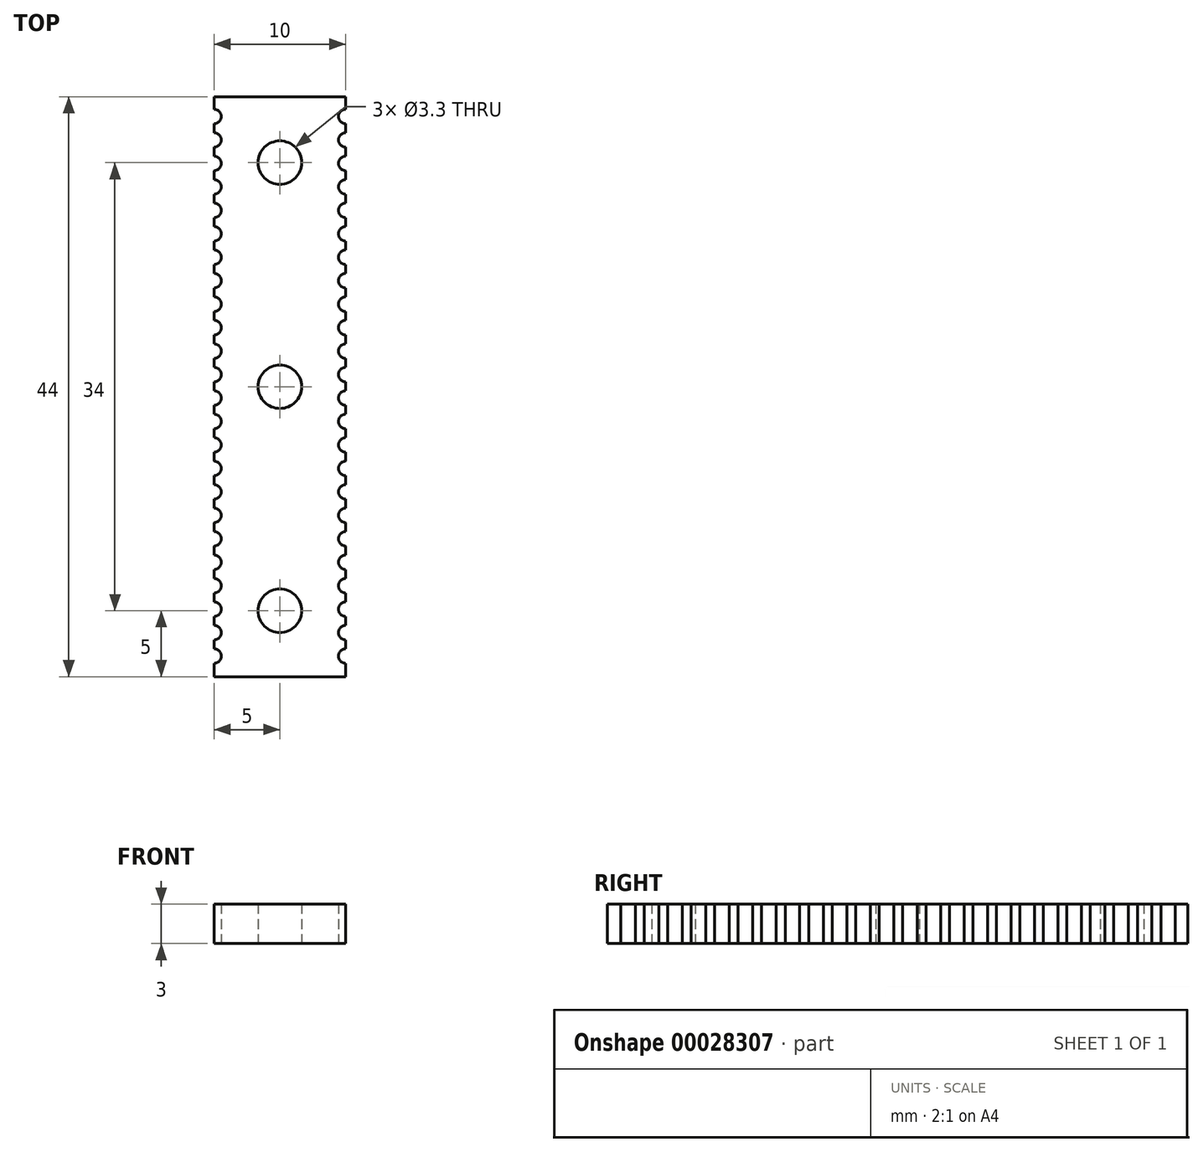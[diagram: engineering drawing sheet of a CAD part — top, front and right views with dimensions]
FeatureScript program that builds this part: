
annotation { "Feature Type Name" : "Feature", "Feature Type Description" : "" }
export const myFeature = defineFeature(function(context is Context, id is Id, definition is map)
    precondition{}
    {
        {
            var Q0;
            Q0=qCreatedBy(makeId("Top.planeOp"),FACE);
            var sketch = newSketch(context, id + "F0", { "sketchPlane" : qUnion([Q0])});
            skLineSegment(sketch, "E0.bottom", {"start": v(0, 0) * mm, "end": v(10, 0) * mm});
            skLineSegment(sketch, "E0.top", {"start": v(0, 44) * mm, "end": v(10, 44) * mm});
            skLineSegment(sketch, "E0.left", {"start": v(0, 0) * mm, "end": v(0, 44) * mm});
            skLineSegment(sketch, "E0.right", {"start": v(10, 0) * mm, "end": v(10, 44) * mm});
            skCircle(sketch, "E1", {"center": v(0, 42.5) * mm, "radius": 0.55 * mm});
            skCircle(sketch, "E2.0.1.0", {"center": v(0, 40.72) * mm, "radius": 0.55 * mm});
            skCircle(sketch, "E2.0.2.0", {"center": v(0, 38.94) * mm, "radius": 0.55 * mm});
            skCircle(sketch, "E2.0.3.0", {"center": v(0, 37.16) * mm, "radius": 0.55 * mm});
            skCircle(sketch, "E2.0.4.0", {"center": v(0, 35.38) * mm, "radius": 0.55 * mm});
            skCircle(sketch, "E2.0.5.0", {"center": v(0, 33.6) * mm, "radius": 0.55 * mm});
            skCircle(sketch, "E2.0.6.0", {"center": v(0, 31.82) * mm, "radius": 0.55 * mm});
            skCircle(sketch, "E2.0.7.0", {"center": v(0, 30.04) * mm, "radius": 0.55 * mm});
            skCircle(sketch, "E2.0.8.0", {"center": v(0, 28.26) * mm, "radius": 0.55 * mm});
            skCircle(sketch, "E2.0.9.0", {"center": v(0, 26.48) * mm, "radius": 0.55 * mm});
            skCircle(sketch, "E2.0.10.0", {"center": v(0, 24.7) * mm, "radius": 0.55 * mm});
            skCircle(sketch, "E2.0.11.0", {"center": v(0, 22.92) * mm, "radius": 0.55 * mm});
            skCircle(sketch, "E2.0.12.0", {"center": v(0, 21.14) * mm, "radius": 0.55 * mm});
            skCircle(sketch, "E2.0.13.0", {"center": v(0, 19.36) * mm, "radius": 0.55 * mm});
            skCircle(sketch, "E2.0.14.0", {"center": v(0, 17.58) * mm, "radius": 0.55 * mm});
            skCircle(sketch, "E2.0.15.0", {"center": v(0, 15.8) * mm, "radius": 0.55 * mm});
            skCircle(sketch, "E2.0.16.0", {"center": v(0, 14.02) * mm, "radius": 0.55 * mm});
            skCircle(sketch, "E2.0.17.0", {"center": v(0, 12.24) * mm, "radius": 0.55 * mm});
            skCircle(sketch, "E2.0.18.0", {"center": v(0, 10.46) * mm, "radius": 0.55 * mm});
            skCircle(sketch, "E2.0.19.0", {"center": v(0, 8.68) * mm, "radius": 0.55 * mm});
            skCircle(sketch, "E2.0.20.0", {"center": v(0, 6.9) * mm, "radius": 0.55 * mm});
            skCircle(sketch, "E2.0.21.0", {"center": v(0, 5.12) * mm, "radius": 0.55 * mm});
            skCircle(sketch, "E2.1.0.0", {"center": v(10, 42.5) * mm, "radius": 0.55 * mm});
            skCircle(sketch, "E2.1.1.0", {"center": v(10, 40.72) * mm, "radius": 0.55 * mm});
            skCircle(sketch, "E2.1.2.0", {"center": v(10, 38.94) * mm, "radius": 0.55 * mm});
            skCircle(sketch, "E2.1.3.0", {"center": v(10, 37.16) * mm, "radius": 0.55 * mm});
            skCircle(sketch, "E2.1.4.0", {"center": v(10, 35.38) * mm, "radius": 0.55 * mm});
            skCircle(sketch, "E2.1.5.0", {"center": v(10, 33.6) * mm, "radius": 0.55 * mm});
            skCircle(sketch, "E2.1.6.0", {"center": v(10, 31.82) * mm, "radius": 0.55 * mm});
            skCircle(sketch, "E2.1.7.0", {"center": v(10, 30.04) * mm, "radius": 0.55 * mm});
            skCircle(sketch, "E2.1.8.0", {"center": v(10, 28.26) * mm, "radius": 0.55 * mm});
            skCircle(sketch, "E2.1.9.0", {"center": v(10, 26.48) * mm, "radius": 0.55 * mm});
            skCircle(sketch, "E2.1.10.0", {"center": v(10, 24.7) * mm, "radius": 0.55 * mm});
            skCircle(sketch, "E2.1.11.0", {"center": v(10, 22.92) * mm, "radius": 0.55 * mm});
            skCircle(sketch, "E2.1.12.0", {"center": v(10, 21.14) * mm, "radius": 0.55 * mm});
            skCircle(sketch, "E2.1.13.0", {"center": v(10, 19.36) * mm, "radius": 0.55 * mm});
            skCircle(sketch, "E2.1.14.0", {"center": v(10, 17.58) * mm, "radius": 0.55 * mm});
            skCircle(sketch, "E2.1.15.0", {"center": v(10, 15.8) * mm, "radius": 0.55 * mm});
            skCircle(sketch, "E2.1.16.0", {"center": v(10, 14.02) * mm, "radius": 0.55 * mm});
            skCircle(sketch, "E2.1.17.0", {"center": v(10, 12.24) * mm, "radius": 0.55 * mm});
            skCircle(sketch, "E2.1.18.0", {"center": v(10, 10.46) * mm, "radius": 0.55 * mm});
            skCircle(sketch, "E2.1.19.0", {"center": v(10, 8.68) * mm, "radius": 0.55 * mm});
            skCircle(sketch, "E2.1.20.0", {"center": v(10, 6.9) * mm, "radius": 0.55 * mm});
            skCircle(sketch, "E2.1.21.0", {"center": v(10, 5.12) * mm, "radius": 0.55 * mm});
            skLineSegment(sketch, "E2.direction1", {"start": v(0, 42.5) * mm, "end": v(10, 42.5) * mm, "construction": true});
            skLineSegment(sketch, "E2.direction2", {"start": v(0, 42.5) * mm, "end": v(0, 40.72) * mm, "construction": true});
            skCircle(sketch, "E3.0.0.22", {"center": v(0, 3.34) * mm, "radius": 0.55 * mm});
            skCircle(sketch, "E3.0.0.23", {"center": v(0, 1.56) * mm, "radius": 0.55 * mm});
            skCircle(sketch, "E3.0.1.22", {"center": v(10, 3.34) * mm, "radius": 0.55 * mm});
            skCircle(sketch, "E3.0.1.23", {"center": v(10, 1.56) * mm, "radius": 0.55 * mm});
            skSolve(sketch);
        }
        {
            var Q0;
            {var subQ102=sQuery(id+"F0.wireOp",EDGE,"E0.bottom");Q0=makeQuery(id+"F0.imprint","IMPRINT",FACE,{"disambiguationData":[TD([[makeQuery(id+"F0.imprint","IMPRINT",EDGE,{"derivedFrom":subQ102}),1.0]])]});}
            var sketch = newSketch(context, id + "F1", { "sketchPlane" : qUnion([Q0])});
            skSolve(sketch);
        }
        {
            var Q0;
            Q0 = qSketchRegion(id + "F1", true);
            var Q1;
            {var subQ102=sQuery(id+"F0.wireOp",EDGE,"E0.bottom");Q1=makeQuery(id+"F0.imprint","IMPRINT",FACE,{"disambiguationData":[TD([[makeQuery(id+"F0.imprint","IMPRINT",EDGE,{"derivedFrom":subQ102}),1.0]])]});}
            extrude(context, id + "F2", {"entities" : qUnion([Q0, Q1]), "depth" : 3 * mm});
        }
        {
            var Q0;
            Q0=makeQuery(id+"F2.opExtrude","CAP_FACE",FACE,{"disambiguationData":[OSD([sQuery(id+"F0.wireOp",EDGE,"E0.bottom"),sQuery(id+"F0.wireOp",EDGE,"E0.top"),sQuery(id+"F0.wireOp",EDGE,"E0.left"),sQuery(id+"F0.wireOp",EDGE,"E0.right"),sQuery(id+"F0.wireOp",EDGE,"E1"),sQuery(id+"F0.wireOp",EDGE,"E2.0.1.0"),sQuery(id+"F0.wireOp",EDGE,"E2.0.2.0"),sQuery(id+"F0.wireOp",EDGE,"E2.0.3.0"),sQuery(id+"F0.wireOp",EDGE,"E2.0.4.0"),sQuery(id+"F0.wireOp",EDGE,"E2.0.5.0"),sQuery(id+"F0.wireOp",EDGE,"E2.0.6.0"),sQuery(id+"F0.wireOp",EDGE,"E2.0.7.0"),sQuery(id+"F0.wireOp",EDGE,"E2.0.8.0"),sQuery(id+"F0.wireOp",EDGE,"E2.0.9.0"),sQuery(id+"F0.wireOp",EDGE,"E2.0.10.0"),sQuery(id+"F0.wireOp",EDGE,"E2.0.11.0"),sQuery(id+"F0.wireOp",EDGE,"E2.0.12.0"),sQuery(id+"F0.wireOp",EDGE,"E2.0.13.0"),sQuery(id+"F0.wireOp",EDGE,"E2.0.14.0"),sQuery(id+"F0.wireOp",EDGE,"E2.0.15.0"),sQuery(id+"F0.wireOp",EDGE,"E2.0.16.0"),sQuery(id+"F0.wireOp",EDGE,"E2.0.17.0"),sQuery(id+"F0.wireOp",EDGE,"E2.0.18.0"),sQuery(id+"F0.wireOp",EDGE,"E2.0.19.0"),sQuery(id+"F0.wireOp",EDGE,"E2.0.20.0"),sQuery(id+"F0.wireOp",EDGE,"E2.0.21.0"),sQuery(id+"F0.wireOp",EDGE,"E2.1.0.0"),sQuery(id+"F0.wireOp",EDGE,"E2.1.1.0"),sQuery(id+"F0.wireOp",EDGE,"E2.1.2.0"),sQuery(id+"F0.wireOp",EDGE,"E2.1.3.0"),sQuery(id+"F0.wireOp",EDGE,"E2.1.4.0"),sQuery(id+"F0.wireOp",EDGE,"E2.1.5.0"),sQuery(id+"F0.wireOp",EDGE,"E2.1.6.0"),sQuery(id+"F0.wireOp",EDGE,"E2.1.7.0"),sQuery(id+"F0.wireOp",EDGE,"E2.1.8.0"),sQuery(id+"F0.wireOp",EDGE,"E2.1.9.0"),sQuery(id+"F0.wireOp",EDGE,"E2.1.10.0"),sQuery(id+"F0.wireOp",EDGE,"E2.1.11.0"),sQuery(id+"F0.wireOp",EDGE,"E2.1.12.0"),sQuery(id+"F0.wireOp",EDGE,"E2.1.13.0"),sQuery(id+"F0.wireOp",EDGE,"E2.1.14.0"),sQuery(id+"F0.wireOp",EDGE,"E2.1.15.0"),sQuery(id+"F0.wireOp",EDGE,"E2.1.16.0"),sQuery(id+"F0.wireOp",EDGE,"E2.1.17.0"),sQuery(id+"F0.wireOp",EDGE,"E2.1.18.0"),sQuery(id+"F0.wireOp",EDGE,"E2.1.19.0"),sQuery(id+"F0.wireOp",EDGE,"E2.1.20.0"),sQuery(id+"F0.wireOp",EDGE,"E2.1.21.0")])],"isStart":false});
            var sketch = newSketch(context, id + "F3", { "sketchPlane" : qUnion([Q0])});
            skLineSegment(sketch, "E4", {"start": v(5, 0) * mm, "end": v(5, 44) * mm, "construction": true});
            skPoint(sketch, "E5", {"position": v(5, 5) * mm});
            skPoint(sketch, "E6", {"position": v(5, 39) * mm});
            skPoint(sketch, "E7", {"position": v(5, 22) * mm});
            skSolve(sketch);
        }
        {
            var Q0;
            Q0=sQuery(id+"F3.wireOp",VERTEX,"E5");
            var Q1;
            Q1=sQuery(id+"F3.wireOp",VERTEX,"E7");
            var Q2;
            Q2=sQuery(id+"F3.wireOp",VERTEX,"E6");
            var Q3;
            Q3=makeQuery(id+"F2.opExtrude","SWEPT_BODY",BODY,{"disambiguationData":[OSD([sQuery(id+"F0.wireOp",EDGE,"E0.bottom"),sQuery(id+"F0.wireOp",EDGE,"E0.top"),sQuery(id+"F0.wireOp",EDGE,"E0.left"),sQuery(id+"F0.wireOp",EDGE,"E0.right"),sQuery(id+"F0.wireOp",EDGE,"E1"),sQuery(id+"F0.wireOp",EDGE,"E2.0.1.0"),sQuery(id+"F0.wireOp",EDGE,"E2.0.2.0"),sQuery(id+"F0.wireOp",EDGE,"E2.0.3.0"),sQuery(id+"F0.wireOp",EDGE,"E2.0.4.0"),sQuery(id+"F0.wireOp",EDGE,"E2.0.5.0"),sQuery(id+"F0.wireOp",EDGE,"E2.0.6.0"),sQuery(id+"F0.wireOp",EDGE,"E2.0.7.0"),sQuery(id+"F0.wireOp",EDGE,"E2.0.8.0"),sQuery(id+"F0.wireOp",EDGE,"E2.0.9.0"),sQuery(id+"F0.wireOp",EDGE,"E2.0.10.0"),sQuery(id+"F0.wireOp",EDGE,"E2.0.11.0"),sQuery(id+"F0.wireOp",EDGE,"E2.0.12.0"),sQuery(id+"F0.wireOp",EDGE,"E2.0.13.0"),sQuery(id+"F0.wireOp",EDGE,"E2.0.14.0"),sQuery(id+"F0.wireOp",EDGE,"E2.0.15.0"),sQuery(id+"F0.wireOp",EDGE,"E2.0.16.0"),sQuery(id+"F0.wireOp",EDGE,"E2.0.17.0"),sQuery(id+"F0.wireOp",EDGE,"E2.0.18.0"),sQuery(id+"F0.wireOp",EDGE,"E2.0.19.0"),sQuery(id+"F0.wireOp",EDGE,"E2.0.20.0"),sQuery(id+"F0.wireOp",EDGE,"E2.0.21.0"),sQuery(id+"F0.wireOp",EDGE,"E2.1.0.0"),sQuery(id+"F0.wireOp",EDGE,"E2.1.1.0"),sQuery(id+"F0.wireOp",EDGE,"E2.1.2.0"),sQuery(id+"F0.wireOp",EDGE,"E2.1.3.0"),sQuery(id+"F0.wireOp",EDGE,"E2.1.4.0"),sQuery(id+"F0.wireOp",EDGE,"E2.1.5.0"),sQuery(id+"F0.wireOp",EDGE,"E2.1.6.0"),sQuery(id+"F0.wireOp",EDGE,"E2.1.7.0"),sQuery(id+"F0.wireOp",EDGE,"E2.1.8.0"),sQuery(id+"F0.wireOp",EDGE,"E2.1.9.0"),sQuery(id+"F0.wireOp",EDGE,"E2.1.10.0"),sQuery(id+"F0.wireOp",EDGE,"E2.1.11.0"),sQuery(id+"F0.wireOp",EDGE,"E2.1.12.0"),sQuery(id+"F0.wireOp",EDGE,"E2.1.13.0"),sQuery(id+"F0.wireOp",EDGE,"E2.1.14.0"),sQuery(id+"F0.wireOp",EDGE,"E2.1.15.0"),sQuery(id+"F0.wireOp",EDGE,"E2.1.16.0"),sQuery(id+"F0.wireOp",EDGE,"E2.1.17.0"),sQuery(id+"F0.wireOp",EDGE,"E2.1.18.0"),sQuery(id+"F0.wireOp",EDGE,"E2.1.19.0"),sQuery(id+"F0.wireOp",EDGE,"E2.1.20.0"),sQuery(id+"F0.wireOp",EDGE,"E2.1.21.0")])]});
            hole(context, id + "F4", {"style" : HoleStyle.SIMPLE, "holeDiameter" : 3.3 * mm, "endStyle" : HoleEndStyle.THROUGH, "locations" : qUnion([Q0, Q1, Q2]), "scope" : qUnion([Q3])});
        }
    });
